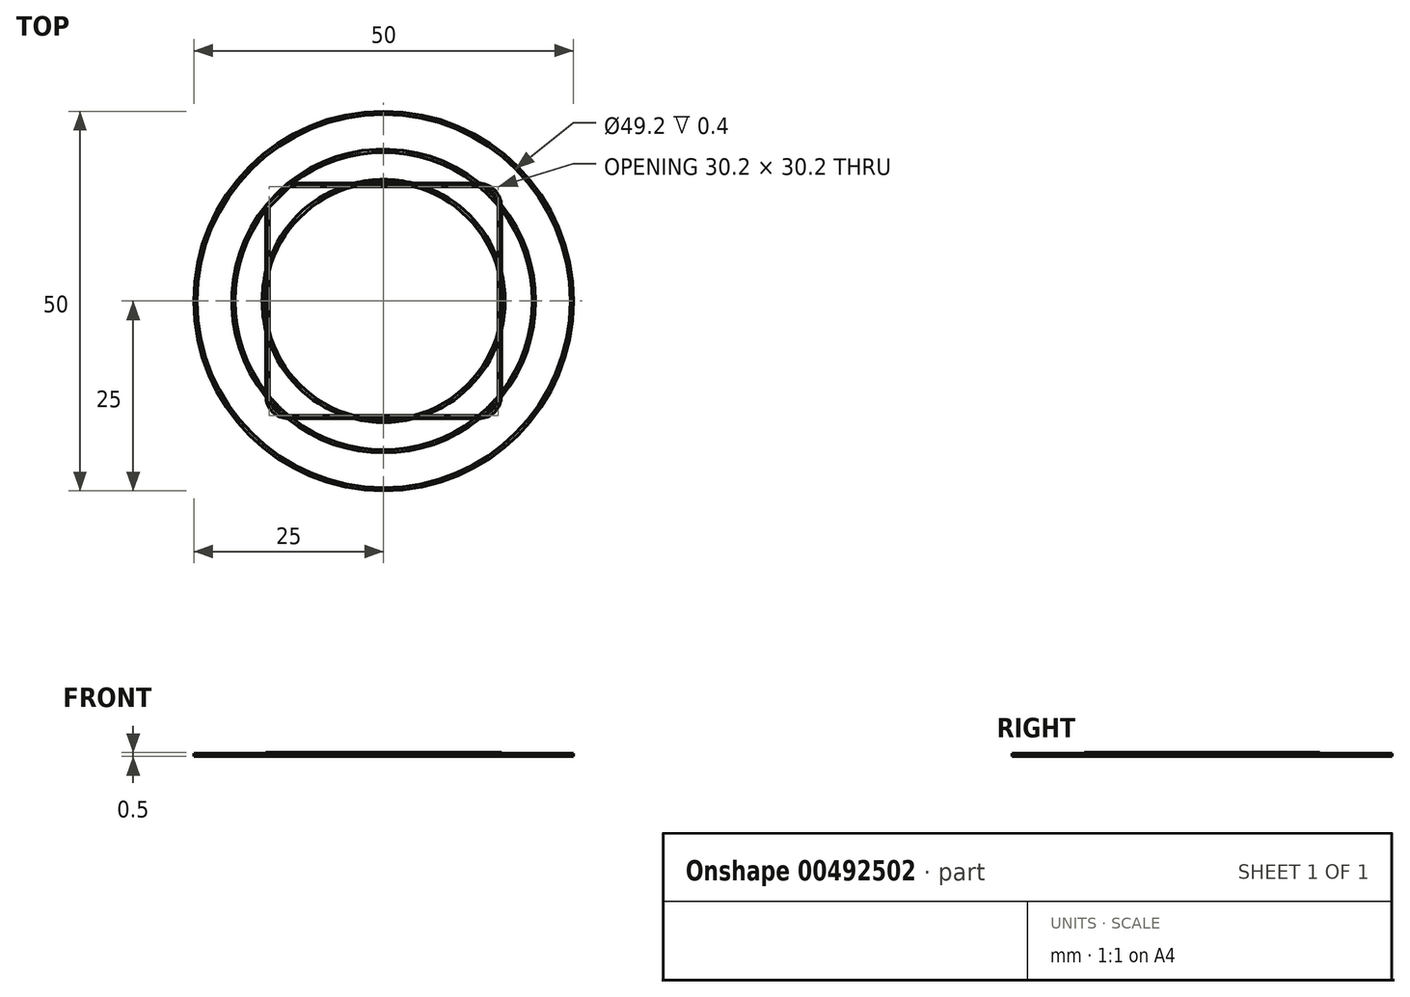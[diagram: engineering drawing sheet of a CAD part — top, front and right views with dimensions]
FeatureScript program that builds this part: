
annotation { "Feature Type Name" : "Feature", "Feature Type Description" : "" }
export const myFeature = defineFeature(function(context is Context, id is Id, definition is map)
    precondition{}
    {
        {
            var Q0;
            Q0=qCreatedBy(makeId("Top.planeOp"),FACE);
            var sketch = newSketch(context, id + "F0", { "sketchPlane" : qUnion([Q0])});
            skLineSegment(sketch, "E0.bottom", {"start": v(12.5, 15.5) * mm, "end": v(-12.5, 15.5) * mm});
            skLineSegment(sketch, "E0.top", {"start": v(12.5, -15.5) * mm, "end": v(-12.5, -15.5) * mm});
            skLineSegment(sketch, "E0.left", {"start": v(15.5, 12.5) * mm, "end": v(15.5, -12.5) * mm});
            skLineSegment(sketch, "E0.right", {"start": v(-15.5, 12.5) * mm, "end": v(-15.5, -12.5) * mm});
            skPoint(sketch, "E0.middle", {"position": v(0, 0) * mm});
            skPoint(sketch, "E1.visualSharp", {"position": v(-15.5, -15.5) * mm});
            skArc(sketch, "E1.filletArc", {"start": v(-15.5, -12.5) * mm, "mid": v(-14.62, -14.62) * mm, "end": v(-12.5, -15.5) * mm});
            skPoint(sketch, "E2.visualSharp", {"position": v(15.5, -15.5) * mm});
            skArc(sketch, "E2.filletArc", {"start": v(12.5, -15.5) * mm, "mid": v(14.62, -14.62) * mm, "end": v(15.5, -12.5) * mm});
            skPoint(sketch, "E3.visualSharp", {"position": v(15.5, 15.5) * mm});
            skArc(sketch, "E3.filletArc", {"start": v(15.5, 12.5) * mm, "mid": v(14.62, 14.62) * mm, "end": v(12.5, 15.5) * mm});
            skLineSegment(sketch, "E4", {"start": v(-15.5, 12.5) * mm, "end": v(-12.5, 15.5) * mm});
            skLineSegment(sketch, "E5.0", {"start": v(12.5, -15.1) * mm, "end": v(-12.5, -15.1) * mm});
            skArc(sketch, "E5.1", {"start": v(-15.1, -12.5) * mm, "mid": v(-14.34, -14.34) * mm, "end": v(-12.5, -15.1) * mm});
            skArc(sketch, "E5.2", {"start": v(12.5, -15.1) * mm, "mid": v(14.34, -14.34) * mm, "end": v(15.1, -12.5) * mm});
            skLineSegment(sketch, "E5.3", {"start": v(-15.1, 12.33) * mm, "end": v(-15.1, -12.5) * mm});
            skLineSegment(sketch, "E5.4", {"start": v(15.1, 12.5) * mm, "end": v(15.1, -12.5) * mm});
            skArc(sketch, "E5.5", {"start": v(15.1, 12.5) * mm, "mid": v(14.34, 14.34) * mm, "end": v(12.5, 15.1) * mm});
            skLineSegment(sketch, "E5.6", {"start": v(12.5, 15.1) * mm, "end": v(-12.33, 15.1) * mm});
            skLineSegment(sketch, "E5.7", {"start": v(-15.1, 12.33) * mm, "end": v(-12.33, 15.1) * mm});
            skSolve(sketch);
        }
        {
            var Q0;
            Q0=makeQuery(id+"F0.imprint","IMPRINT",FACE,{"disambiguationData":[TD([[makeQuery(id+"F0.imprint","IMPRINT",EDGE,{"derivedFrom":sQuery(id+"F0.wireOp",EDGE,"E0.bottom")}),1.0]])]});
            extrude(context, id + "F1", {"entities" : qUnion([Q0]), "depth" : 0.5 * mm});
        }
        {
            var Q0;
            Q0=qCreatedBy(makeId("Top.planeOp"),FACE);
            var sketch = newSketch(context, id + "F2", { "sketchPlane" : qUnion([Q0])});
            skCircle(sketch, "E6", {"center": v(0, 0) * mm, "radius": 16 * mm});
            skCircle(sketch, "E7", {"center": v(0, 0) * mm, "radius": 20 * mm});
            skCircle(sketch, "E8.0", {"center": v(0, 0) * mm, "radius": 19.6 * mm});
            skCircle(sketch, "E9.0", {"center": v(0, 0) * mm, "radius": 15.6 * mm});
            skSolve(sketch);
        }
        {
            var Q0;
            Q0=makeQuery(id+"F2.imprint","IMPRINT",FACE,{"disambiguationData":[TD([[makeQuery(id+"F2.imprint","IMPRINT",EDGE,{"derivedFrom":sQuery(id+"F2.wireOp",EDGE,"E7")}),1.0]])]});
            var Q1;
            Q1=makeQuery(id+"F2.imprint","IMPRINT",FACE,{"disambiguationData":[TD([[makeQuery(id+"F2.imprint","IMPRINT",EDGE,{"derivedFrom":sQuery(id+"F2.wireOp",EDGE,"E6")}),1.0]])]});
            extrude(context, id + "F3", {"entities" : qUnion([Q0, Q1]), "operationType" : NewBodyOperationType.ADD, "depth" : 0.4 * mm});
        }
        {
            var Q0;
            Q0=qCreatedBy(makeId("Top.planeOp"),FACE);
            var sketch = newSketch(context, id + "F4", { "sketchPlane" : qUnion([Q0])});
            skCircle(sketch, "E10", {"center": v(0, 0) * mm, "radius": 25 * mm});
            skCircle(sketch, "E11.0", {"center": v(0, 0) * mm, "radius": 24.6 * mm});
            skSolve(sketch);
        }
        {
            var Q0;
            Q0=makeQuery(id+"F4.imprint","IMPRINT",FACE,{"disambiguationData":[TD([[makeQuery(id+"F4.imprint","IMPRINT",EDGE,{"derivedFrom":sQuery(id+"F4.wireOp",EDGE,"E10")}),1.0]])]});
            extrude(context, id + "F5", {"entities" : qUnion([Q0]), "depth" : 0.4 * mm});
        }
    });
